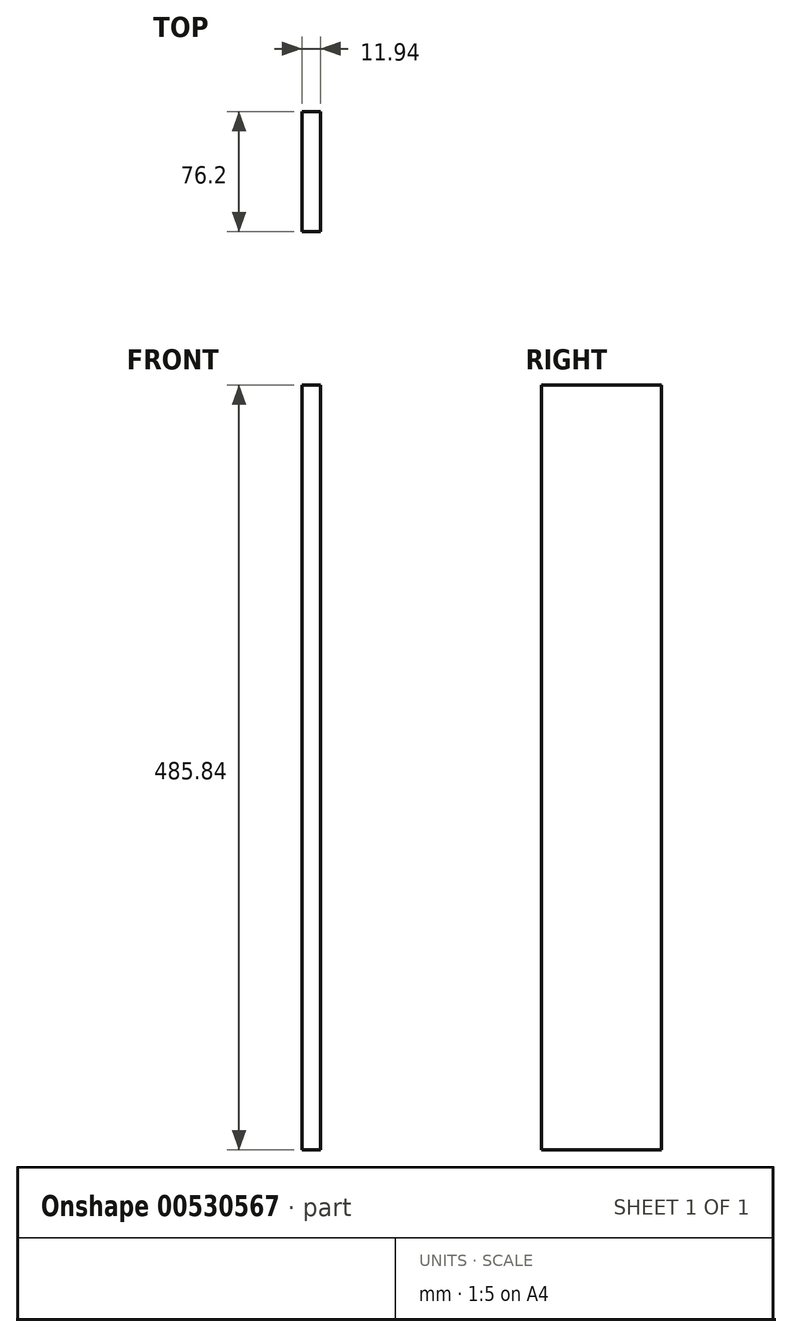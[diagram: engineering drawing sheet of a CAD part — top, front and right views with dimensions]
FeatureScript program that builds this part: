
annotation { "Feature Type Name" : "Feature", "Feature Type Description" : "" }
export const myFeature = defineFeature(function(context is Context, id is Id, definition is map)
    precondition{}
    {
        {
            var Q0;
            Q0=qCreatedBy(makeId("Right.planeOp"),FACE);
            var sketch = newSketch(context, id + "F0", { "sketchPlane" : qUnion([Q0])});
            skLineSegment(sketch, "E0.bottom", {"start": v(0, 0) * mm, "end": v(-76.2, 0) * mm});
            skLineSegment(sketch, "E0.top", {"start": v(0, 485.84) * mm, "end": v(-76.2, 485.84) * mm});
            skLineSegment(sketch, "E0.left", {"start": v(0, 0) * mm, "end": v(0, 485.84) * mm});
            skLineSegment(sketch, "E0.right", {"start": v(-76.2, 0) * mm, "end": v(-76.2, 485.84) * mm});
            skSolve(sketch);
        }
        {
            var Q0;
            Q0 = qSketchRegion(id + "F0", true);
            extrude(context, id + "F1", {"entities" : qUnion([Q0]), "depth" : 11.94 * mm, "offsetDistance" : 25.4 * mm});
        }
    });
